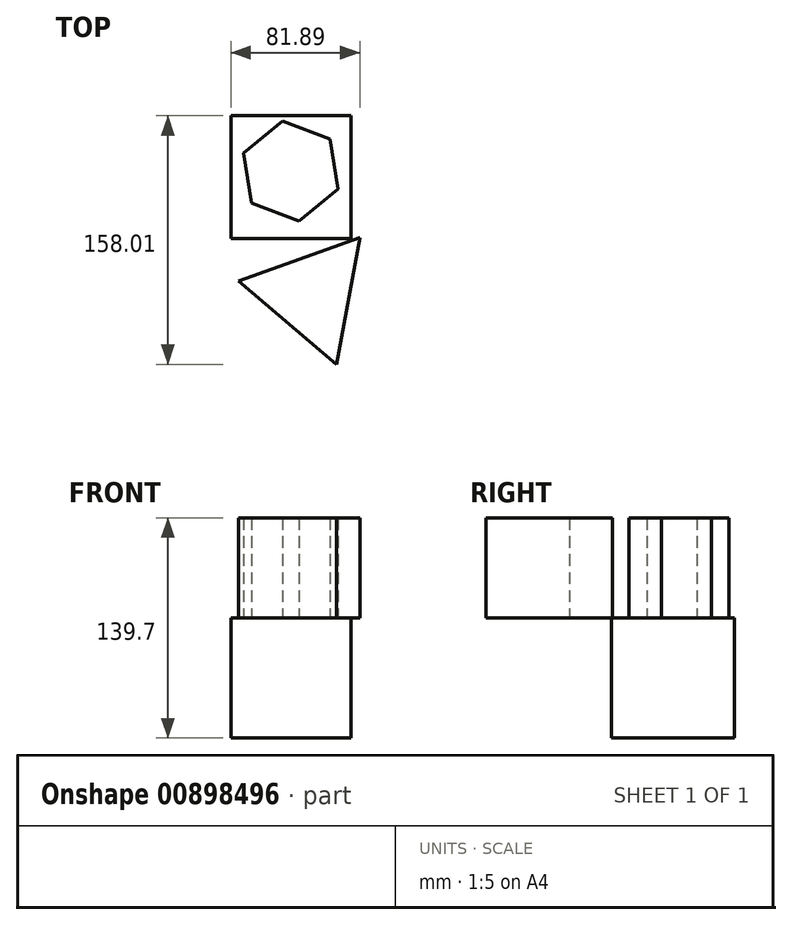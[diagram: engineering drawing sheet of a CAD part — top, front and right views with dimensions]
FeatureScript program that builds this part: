
annotation { "Feature Type Name" : "Feature", "Feature Type Description" : "" }
export const myFeature = defineFeature(function(context is Context, id is Id, definition is map)
    precondition{}
    {
        {
            var Q0;
            Q0=qCreatedBy(makeId("Top.planeOp"),FACE);
            var sketch = newSketch(context, id + "F0", { "sketchPlane" : qUnion([Q0])});
            skLineSegment(sketch, "E0.bottom", {"start": v(0, 0) * mm, "end": v(76.18, 0) * mm});
            skLineSegment(sketch, "E0.top", {"start": v(0, 78.1) * mm, "end": v(76.18, 78.1) * mm});
            skLineSegment(sketch, "E0.left", {"start": v(0, 0) * mm, "end": v(0, 78.1) * mm});
            skLineSegment(sketch, "E0.right", {"start": v(76.18, 0) * mm, "end": v(76.18, 78.1) * mm});
            skSolve(sketch);
        }
        {
            var Q0;
            Q0 = qSketchRegion(id + "F0", true);
            extrude(context, id + "F1", {"entities" : qUnion([Q0]), "depth" : 25.4 * mm, "offsetDistance" : 25.4 * mm});
        }
        {
            var Q0;
            Q0=makeQuery(id+"F1.opExtrude","CAP_FACE",FACE,{"disambiguationData":[OSD([sQuery(id+"F0.wireOp",EDGE,"E0.bottom"),sQuery(id+"F0.wireOp",EDGE,"E0.top"),sQuery(id+"F0.wireOp",EDGE,"E0.left"),sQuery(id+"F0.wireOp",EDGE,"E0.right")])],"isStart":false});
            var sketch = newSketch(context, id + "F2", { "sketchPlane" : qUnion([Q0])});
            skSolve(sketch);
        }
        {
            var Q0;
            Q0=makeQuery(id+"F2.imprint","IMPRINT",FACE,{"disambiguationData":[TD([[makeQuery(id+"F2.imprint","IMPRINT",EDGE,{"derivedFrom":makeQuery(id+"F1.opExtrude","CAP_EDGE",EDGE,{"disambiguationData":[OSD([sQuery(id+"F0.wireOp",EDGE,"E0.bottom")])],"isStart":false})}),1.0]])]});
            extrude(context, id + "F3", {"entities" : qUnion([Q0]), "operationType" : NewBodyOperationType.ADD, "depth" : 50.8 * mm, "offsetDistance" : 25.4 * mm});
        }
        {
            var Q0;
            Q0=makeQuery(id+"F3.opExtrude","CAP_FACE",FACE,{"disambiguationData":[OSD([sQuery(id+"F0.wireOp",EDGE,"E0.bottom"),sQuery(id+"F0.wireOp",EDGE,"E0.top"),sQuery(id+"F0.wireOp",EDGE,"E0.left"),sQuery(id+"F0.wireOp",EDGE,"E0.right")])],"isStart":false});
            var sketch = newSketch(context, id + "F4", { "sketchPlane" : qUnion([Q0])});
            skCircle(sketch, "E1.cCircle", {"center": v(51.23, -35.39) * mm, "radius": 47.23 * mm, "construction": true});
            skLineSegment(sketch, "E1.0", {"start": v(67.02, -79.9) * mm, "end": v(4.8, -26.8) * mm});
            skLineSegment(sketch, "E1.1", {"start": v(4.8, -26.8) * mm, "end": v(81.89, 0.54) * mm});
            skLineSegment(sketch, "E1.2", {"start": v(81.89, 0.54) * mm, "end": v(67.02, -79.9) * mm});
            skCircle(sketch, "E2.cCircle", {"center": v(38.09, 42.9) * mm, "radius": 32.15 * mm, "construction": true});
            skPoint(sketch, "E2.cCircle.centerSnap0", {"position": v(38.09, 78.1) * mm});
            skPoint(sketch, "E2.cCircle.perimeterSnap0", {"position": v(43.34, -13.13) * mm});
            skLineSegment(sketch, "E2.0", {"start": v(43.34, 11.18) * mm, "end": v(13.25, 22.49) * mm});
            skPoint(sketch, "E2.0.startSnap0", {"position": v(43.34, -13.13) * mm});
            skLineSegment(sketch, "E2.1", {"start": v(13.25, 22.49) * mm, "end": v(8, 54.2) * mm});
            skLineSegment(sketch, "E2.2", {"start": v(8, 54.2) * mm, "end": v(32.84, 74.6) * mm});
            skLineSegment(sketch, "E2.3", {"start": v(32.84, 74.6) * mm, "end": v(62.93, 63.3) * mm});
            skLineSegment(sketch, "E2.4", {"start": v(62.93, 63.3) * mm, "end": v(68.18, 31.58) * mm});
            skLineSegment(sketch, "E2.5", {"start": v(68.18, 31.58) * mm, "end": v(43.34, 11.18) * mm});
            skSolve(sketch);
        }
        {
            var Q0;
            Q0 = qSketchRegion(id + "F4", true);
            extrude(context, id + "F5", {"entities" : qUnion([Q0]), "operationType" : NewBodyOperationType.ADD, "depth" : 63.5 * mm, "offsetDistance" : 25.4 * mm});
        }
    });
